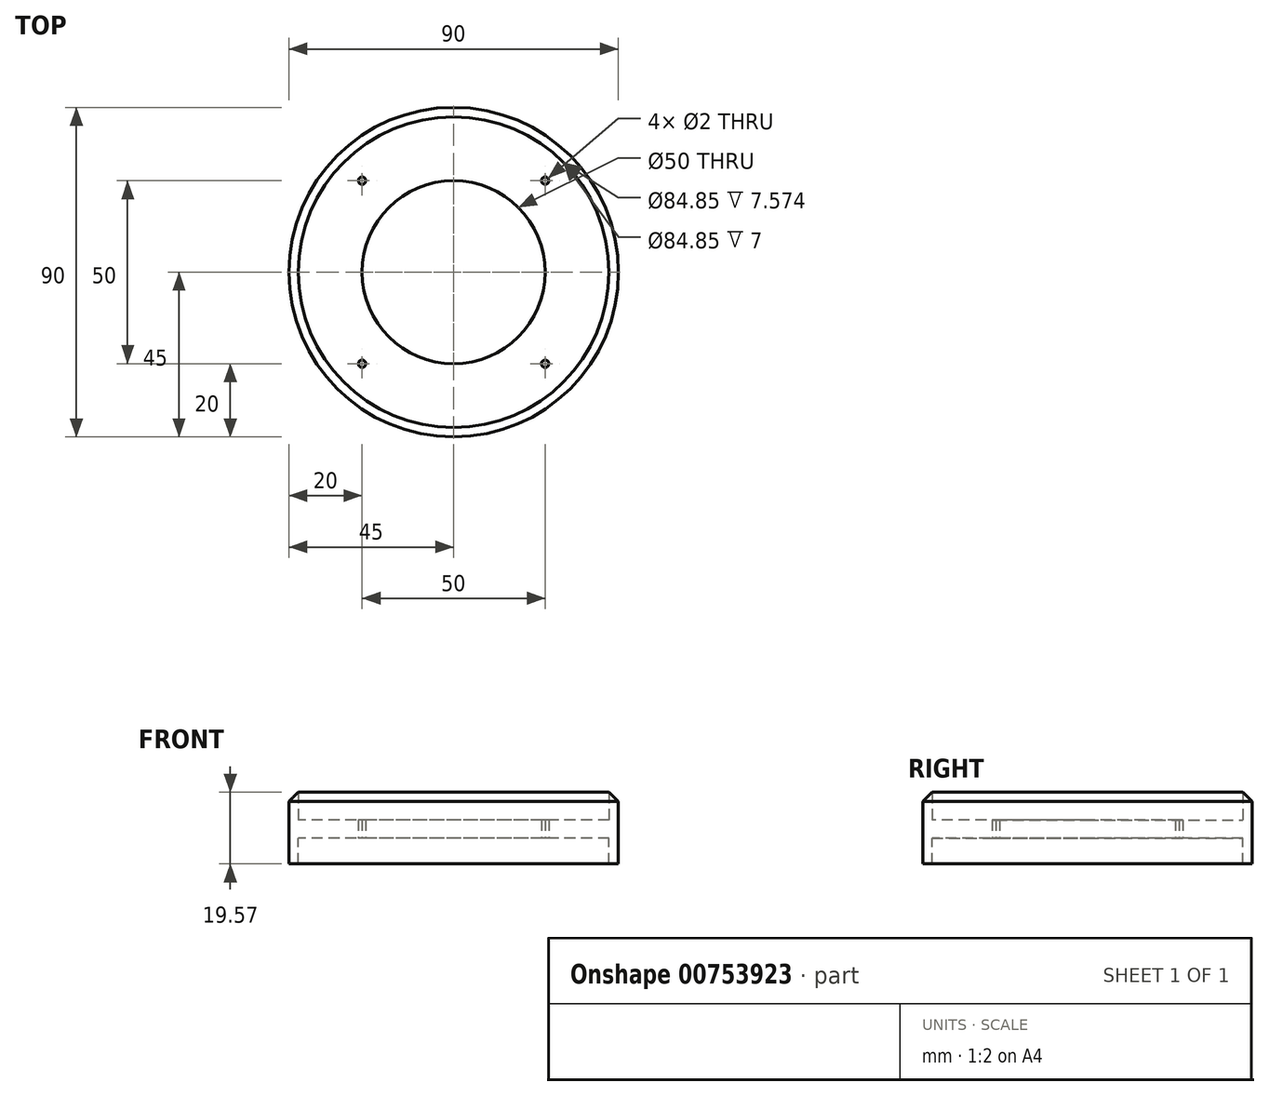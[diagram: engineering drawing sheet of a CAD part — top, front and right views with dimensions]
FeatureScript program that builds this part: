
annotation { "Feature Type Name" : "Feature", "Feature Type Description" : "" }
export const myFeature = defineFeature(function(context is Context, id is Id, definition is map)
    precondition{}
    {
        {
            var Q0;
            Q0=qCreatedBy(makeId("Top.planeOp"),FACE);
            var sketch = newSketch(context, id + "F0", { "sketchPlane" : qUnion([Q0])});
            skLineSegment(sketch, "E0.bottom", {"start": v(30, -30) * mm, "end": v(-30, -30) * mm});
            skLineSegment(sketch, "E0.top", {"start": v(30, 30) * mm, "end": v(-30, 30) * mm});
            skLineSegment(sketch, "E0.left", {"start": v(30, -30) * mm, "end": v(30, 30) * mm});
            skLineSegment(sketch, "E0.right", {"start": v(-30, -30) * mm, "end": v(-30, 30) * mm});
            skPoint(sketch, "E0.middle", {"position": v(0, 0) * mm});
            skCircle(sketch, "E1", {"center": v(0, 0) * mm, "radius": 42.43 * mm});
            skCircle(sketch, "E2", {"center": v(0, 0) * mm, "radius": 25 * mm});
            skLineSegment(sketch, "E3.bottom", {"start": v(25, -25) * mm, "end": v(-25, -25) * mm});
            skLineSegment(sketch, "E3.top", {"start": v(25, 25) * mm, "end": v(-25, 25) * mm});
            skLineSegment(sketch, "E3.left", {"start": v(25, -25) * mm, "end": v(25, 25) * mm});
            skLineSegment(sketch, "E3.right", {"start": v(-25, -25) * mm, "end": v(-25, 25) * mm});
            skCircle(sketch, "E4", {"center": v(25, -25) * mm, "radius": 1 * mm});
            skCircle(sketch, "E5", {"center": v(-25, 25) * mm, "radius": 1 * mm});
            skCircle(sketch, "E6", {"center": v(25, 25) * mm, "radius": 1 * mm});
            skCircle(sketch, "E7", {"center": v(-25, -25) * mm, "radius": 1 * mm});
            skCircle(sketch, "E8", {"center": v(0, 0) * mm, "radius": 45 * mm});
            skSolve(sketch);
        }
        {
            var Q0;
            Q0=makeQuery(id+"F0.imprint","IMPRINT",FACE,{"disambiguationData":[TD([[makeQuery(id+"F0.imprint","IMPRINT",EDGE,{"derivedFrom":sQuery(id+"F0.wireOp",EDGE,"E0.bottom")}),-1.0]])]});
            var Q1;
            {var subQ0=sQuery(id+"F0.wireOp",EDGE,"E3.top");var subQ1=sQuery(id+"F0.wireOp",EDGE,"E2");var subQ2=makeQuery(id+"F0.imprint","INTERSECT",VERTEX,{"derivedFrom":[subQ1,subQ0]});Q1=makeQuery(id+"F0.imprint","IMPRINT",FACE,{"disambiguationData":[TD([[makeQuery(id+"F0.imprint","IMPRINT",EDGE,{"disambiguationData":[TD([[subQ2,1.0]])],"derivedFrom":subQ1}),-1.0]])]});}
            var Q2;
            {var subQ0=sQuery(id+"F0.wireOp",EDGE,"E0.left");Q2=makeQuery(id+"F0.imprint","IMPRINT",FACE,{"disambiguationData":[TD([[makeQuery(id+"F0.imprint","IMPRINT",EDGE,{"derivedFrom":subQ0}),-1.0]])]});}
            var Q3;
            {var subQ0=sQuery(id+"F0.wireOp",EDGE,"E0.bottom");Q3=makeQuery(id+"F0.imprint","IMPRINT",FACE,{"disambiguationData":[TD([[makeQuery(id+"F0.imprint","IMPRINT",EDGE,{"derivedFrom":subQ0}),1.0]])]});}
            var Q4;
            {var subQ0=sQuery(id+"F0.wireOp",EDGE,"E0.right");Q4=makeQuery(id+"F0.imprint","IMPRINT",FACE,{"disambiguationData":[TD([[makeQuery(id+"F0.imprint","IMPRINT",EDGE,{"derivedFrom":subQ0}),1.0]])]});}
            var Q5;
            {var subQ0=sQuery(id+"F0.wireOp",EDGE,"E3.right");var subQ1=sQuery(id+"F0.wireOp",EDGE,"E2");var subQ2=makeQuery(id+"F0.imprint","INTERSECT",VERTEX,{"derivedFrom":[subQ1,subQ0]});Q5=makeQuery(id+"F0.imprint","IMPRINT",FACE,{"disambiguationData":[TD([[makeQuery(id+"F0.imprint","IMPRINT",EDGE,{"disambiguationData":[TD([[subQ2,-1.0]])],"derivedFrom":subQ1}),-1.0]])]});}
            var Q6;
            {var subQ0=sQuery(id+"F0.wireOp",EDGE,"E3.left");var subQ1=sQuery(id+"F0.wireOp",EDGE,"E2");var subQ2=makeQuery(id+"F0.imprint","INTERSECT",VERTEX,{"derivedFrom":[subQ1,subQ0]});Q6=makeQuery(id+"F0.imprint","IMPRINT",FACE,{"disambiguationData":[TD([[makeQuery(id+"F0.imprint","IMPRINT",EDGE,{"disambiguationData":[TD([[subQ2,1.0]])],"derivedFrom":subQ1}),-1.0]])]});}
            var Q7;
            {var subQ0=sQuery(id+"F0.wireOp",EDGE,"E3.top");var subQ1=sQuery(id+"F0.wireOp",EDGE,"E2");var subQ2=makeQuery(id+"F0.imprint","INTERSECT",VERTEX,{"derivedFrom":[subQ1,subQ0]});Q7=makeQuery(id+"F0.imprint","IMPRINT",FACE,{"disambiguationData":[TD([[makeQuery(id+"F0.imprint","IMPRINT",EDGE,{"disambiguationData":[TD([[subQ2,-1.0]])],"derivedFrom":subQ1}),-1.0]])]});}
            var Q8;
            {var subQ0=sQuery(id+"F0.wireOp",EDGE,"E0.top");Q8=makeQuery(id+"F0.imprint","IMPRINT",FACE,{"disambiguationData":[TD([[makeQuery(id+"F0.imprint","IMPRINT",EDGE,{"derivedFrom":subQ0}),-1.0]])]});}
            extrude(context, id + "F1", {"entities" : qUnion([Q0, Q1, Q2, Q3, Q4, Q5, Q6, Q7, Q8]), "depth" : 5 * mm, "offsetDistance" : 25 * mm});
        }
        {
            var Q0;
            Q0=makeQuery(id+"F0.imprint","IMPRINT",FACE,{"disambiguationData":[TD([[makeQuery(id+"F0.imprint","IMPRINT",EDGE,{"derivedFrom":sQuery(id+"F0.wireOp",EDGE,"E8")}),1.0]])]});
            extrude(context, id + "F2", {"entities" : qUnion([Q0]), "operationType" : NewBodyOperationType.ADD, "depth" : 15 * mm, "offsetDistance" : 25 * mm});
        }
        {
            var Q0;
            Q0=makeQuery(id+"F2.opExtrude","CAP_EDGE",EDGE,{"disambiguationData":[OSD([sQuery(id+"F0.wireOp",EDGE,"E8")])],"isStart":false});
            chamfer(context, id + "F3", {"entities" : qUnion([Q0]), "width" : 5 * mm, "tangentPropagation" : true});
        }
        {
            var Q0;
            Q0=makeQuery(id+"F0.imprint","IMPRINT",FACE,{"disambiguationData":[TD([[makeQuery(id+"F0.imprint","IMPRINT",EDGE,{"derivedFrom":sQuery(id+"F0.wireOp",EDGE,"E8")}),1.0]])]});
            extrude(context, id + "F4", {"entities" : qUnion([Q0]), "operationType" : NewBodyOperationType.ADD, "oppositeDirection" : true, "depth" : 4 * mm, "offsetDistance" : 25 * mm});
        }
        {
            var Q0;
            Q0=makeQuery(id+"F0.imprint","IMPRINT",FACE,{"disambiguationData":[TD([[makeQuery(id+"F0.imprint","IMPRINT",EDGE,{"derivedFrom":sQuery(id+"F0.wireOp",EDGE,"E8")}),1.0]])]});
            extrude(context, id + "F5", {"entities" : qUnion([Q0]), "operationType" : NewBodyOperationType.ADD, "oppositeDirection" : true, "depth" : 7 * mm, "offsetDistance" : 25 * mm});
        }
    });
